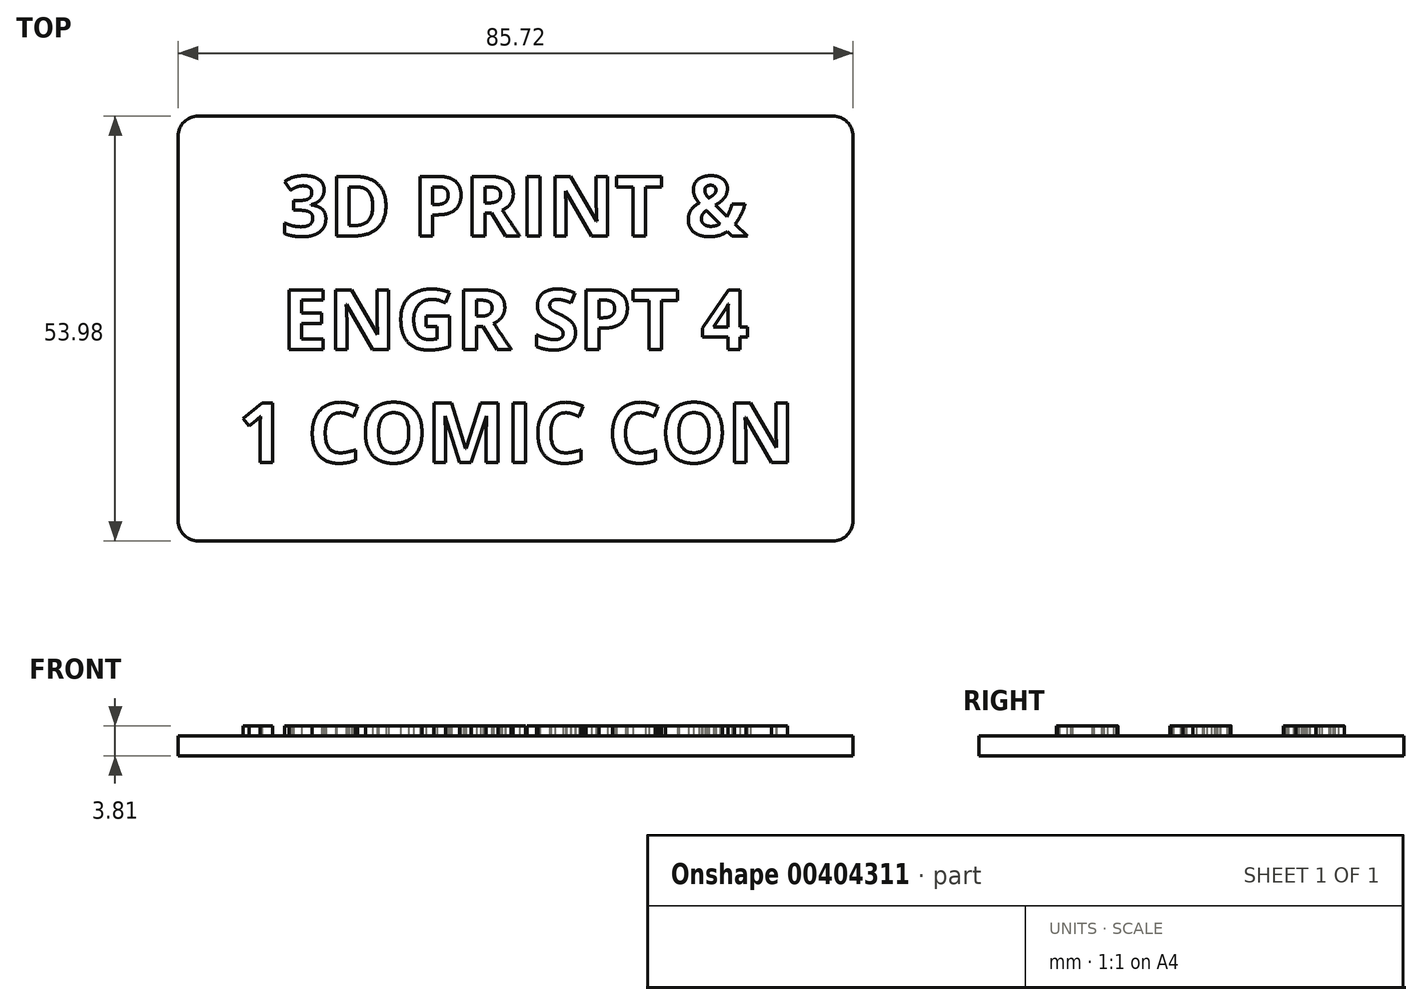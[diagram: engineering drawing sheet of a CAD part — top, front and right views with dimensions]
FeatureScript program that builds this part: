
annotation { "Feature Type Name" : "Feature", "Feature Type Description" : "" }
export const myFeature = defineFeature(function(context is Context, id is Id, definition is map)
    precondition{}
    {
        {
            var Q0;
            Q0=qCreatedBy(makeId("Top.planeOp"),FACE);
            var sketch = newSketch(context, id + "F0", { "sketchPlane" : qUnion([Q0])});
            skLineSegment(sketch, "E0.bottom", {"start": v(40.32, 26.99) * mm, "end": v(-40.32, 26.99) * mm});
            skLineSegment(sketch, "E0.top", {"start": v(40.32, -26.99) * mm, "end": v(-40.32, -26.99) * mm});
            skLineSegment(sketch, "E0.left", {"start": v(42.86, 24.45) * mm, "end": v(42.86, -24.45) * mm});
            skLineSegment(sketch, "E0.right", {"start": v(-42.86, 24.45) * mm, "end": v(-42.86, -24.45) * mm});
            skPoint(sketch, "E0.middle", {"position": v(0, 0) * mm});
            skPoint(sketch, "E1.visualSharp", {"position": v(42.86, 26.99) * mm});
            skArc(sketch, "E1.filletArc", {"start": v(42.86, 24.45) * mm, "mid": v(42.12, 26.24) * mm, "end": v(40.32, 26.99) * mm});
            skPoint(sketch, "E2.visualSharp", {"position": v(42.86, -26.99) * mm});
            skArc(sketch, "E2.filletArc", {"start": v(40.32, -26.99) * mm, "mid": v(42.12, -26.24) * mm, "end": v(42.86, -24.45) * mm});
            skPoint(sketch, "E3.visualSharp", {"position": v(-42.86, -26.99) * mm});
            skArc(sketch, "E3.filletArc", {"start": v(-42.86, -24.45) * mm, "mid": v(-42.12, -26.24) * mm, "end": v(-40.32, -26.99) * mm});
            skPoint(sketch, "E4.visualSharp", {"position": v(-42.86, 26.99) * mm});
            skArc(sketch, "E4.filletArc", {"start": v(-40.32, 26.99) * mm, "mid": v(-42.12, 26.24) * mm, "end": v(-42.86, 24.45) * mm});
            skSolve(sketch);
        }
        {
            var Q0;
            Q0=makeQuery(id+"F0.imprint","IMPRINT",FACE,{"disambiguationData":[TD([[makeQuery(id+"F0.imprint","IMPRINT",EDGE,{"derivedFrom":sQuery(id+"F0.wireOp",EDGE,"E0.bottom")}),1.0]])]});
            extrude(context, id + "F1", {"entities" : qUnion([Q0]), "depth" : 2.54 * mm});
        }
        {
            var Q0;
            Q0=makeQuery(id+"F1.opExtrude","CAP_FACE",FACE,{"disambiguationData":[OSD([sQuery(id+"F0.wireOp",EDGE,"E0.bottom"),sQuery(id+"F0.wireOp",EDGE,"E0.top"),sQuery(id+"F0.wireOp",EDGE,"E0.left"),sQuery(id+"F0.wireOp",EDGE,"E0.right"),sQuery(id+"F0.wireOp",EDGE,"E1.filletArc"),sQuery(id+"F0.wireOp",EDGE,"E2.filletArc"),sQuery(id+"F0.wireOp",EDGE,"E3.filletArc"),sQuery(id+"F0.wireOp",EDGE,"E4.filletArc")])],"isStart":false});
            var sketch = newSketch(context, id + "F2", { "sketchPlane" : qUnion([Q0])});
            skText(sketch, "E5", { "text": "  3D PRINT &\n  ENGR SPT 4\n1 COMIC CON", "fontName": "OpenSans-Bold.ttf"});
            const initialGuessF2  = {"E5": [-0.03524, 0.01175, 1, 0, 0.00762]};
            skSetInitialGuess(sketch, initialGuessF2);
            skSolve(sketch);
        }
        {
            var Q0;
            Q0 = qSketchRegion(id + "F2", true);
            extrude(context, id + "F3", {"entities" : qUnion([Q0]), "operationType" : NewBodyOperationType.ADD, "depth" : 1.27 * mm});
        }
    });
